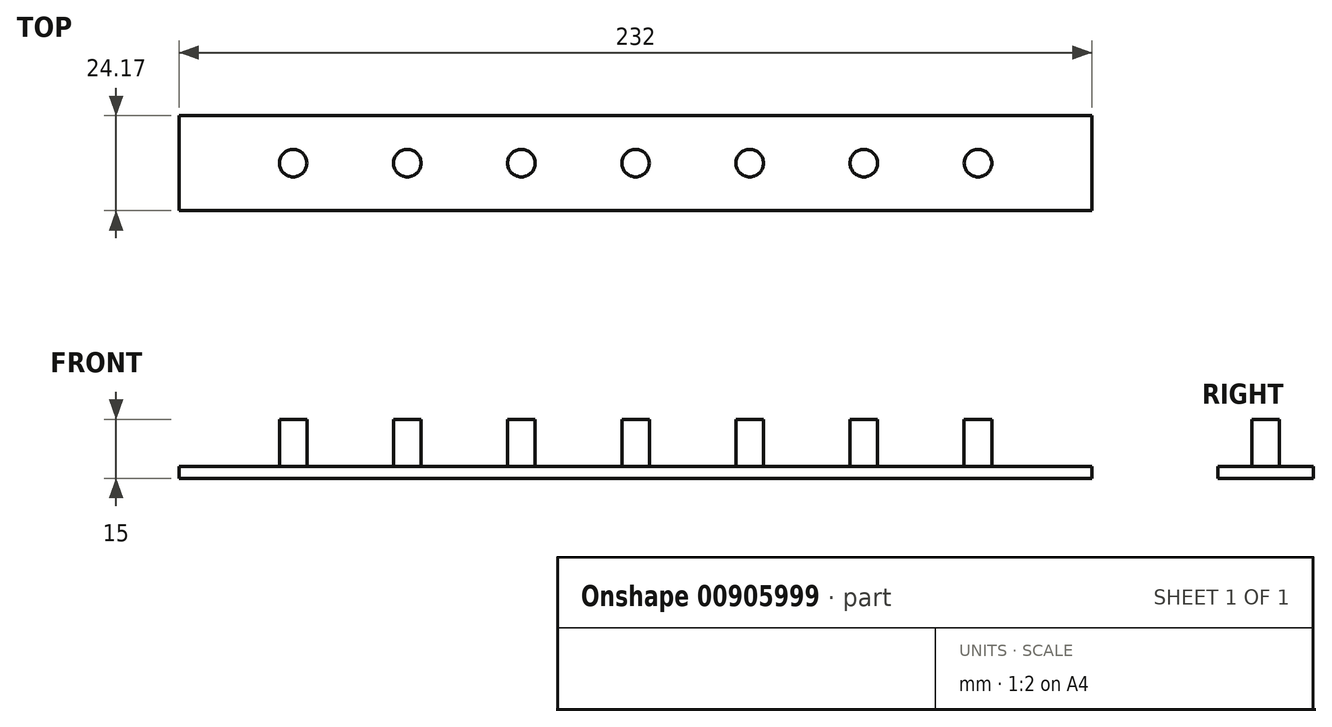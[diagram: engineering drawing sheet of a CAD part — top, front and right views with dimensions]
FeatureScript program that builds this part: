
annotation { "Feature Type Name" : "Feature", "Feature Type Description" : "" }
export const myFeature = defineFeature(function(context is Context, id is Id, definition is map)
    precondition{}
    {
        {
            var Q0;
            Q0=qCreatedBy(makeId("Top.planeOp"),FACE);
            var sketch = newSketch(context, id + "F0", { "sketchPlane" : qUnion([Q0])});
            skLineSegment(sketch, "E0.bottom", {"start": v(-128.67, 31.14) * mm, "end": v(103.33, 31.14) * mm});
            skLineSegment(sketch, "E0.top", {"start": v(-128.67, 6.97) * mm, "end": v(103.33, 6.97) * mm});
            skLineSegment(sketch, "E0.left", {"start": v(-128.67, 31.14) * mm, "end": v(-128.67, 19.05) * mm});
            skLineSegment(sketch, "E0.right", {"start": v(103.33, 31.14) * mm, "end": v(103.33, 19.05) * mm});
            skLineSegment(sketch, "E1", {"start": v(-128.67, 19.05) * mm, "end": v(-128.67, 6.97) * mm});
            skLineSegment(sketch, "E2", {"start": v(103.33, 19.05) * mm, "end": v(103.33, 6.97) * mm});
            skLineSegment(sketch, "E3", {"start": v(-128.67, 19.05) * mm, "end": v(-99.67, 19.05) * mm});
            skLineSegment(sketch, "E4", {"start": v(-12.67, 19.05) * mm, "end": v(16.33, 19.05) * mm});
            skLineSegment(sketch, "E5", {"start": v(-70.67, 19.05) * mm, "end": v(-41.67, 19.05) * mm});
            skLineSegment(sketch, "E6", {"start": v(-41.67, 19.05) * mm, "end": v(-12.67, 19.05) * mm});
            skLineSegment(sketch, "E7", {"start": v(-99.67, 19.05) * mm, "end": v(-70.67, 19.05) * mm});
            skLineSegment(sketch, "E8", {"start": v(45.33, 19.05) * mm, "end": v(74.33, 19.05) * mm});
            skLineSegment(sketch, "E9", {"start": v(16.33, 19.05) * mm, "end": v(45.33, 19.05) * mm});
            skLineSegment(sketch, "E10", {"start": v(74.33, 19.05) * mm, "end": v(103.33, 19.05) * mm});
            skCircle(sketch, "E11", {"center": v(-99.67, 19.05) * mm, "radius": 3.5 * mm});
            skCircle(sketch, "E12", {"center": v(-70.67, 19.05) * mm, "radius": 3.5 * mm});
            skCircle(sketch, "E13", {"center": v(-41.67, 19.05) * mm, "radius": 3.5 * mm});
            skCircle(sketch, "E14", {"center": v(-12.67, 19.05) * mm, "radius": 3.5 * mm});
            skCircle(sketch, "E15", {"center": v(16.33, 19.05) * mm, "radius": 3.5 * mm});
            skCircle(sketch, "E16", {"center": v(45.33, 19.05) * mm, "radius": 3.5 * mm});
            skCircle(sketch, "E17", {"center": v(74.33, 19.05) * mm, "radius": 3.5 * mm});
            skSolve(sketch);
        }
        {
            var Q0;
            Q0=makeQuery(id+"F0.imprint","IMPRINT",FACE,{"disambiguationData":[TD([[makeQuery(id+"F0.imprint","IMPRINT",EDGE,{"derivedFrom":sQuery(id+"F0.wireOp",EDGE,"E0.bottom")}),-1.0]])]});
            var Q1;
            Q1=makeQuery(id+"F0.imprint","IMPRINT",FACE,{"disambiguationData":[TD([[makeQuery(id+"F0.imprint","IMPRINT",EDGE,{"derivedFrom":sQuery(id+"F0.wireOp",EDGE,"E0.top")}),1.0]])]});
            extrude(context, id + "F1", {"entities" : qUnion([Q0, Q1]), "depth" : 3 * mm, "offsetDistance" : 25 * mm});
        }
        {
            var Q0;
            {var subQ0=sQuery(id+"F0.wireOp",EDGE,"E7");var subQ1=sQuery(id+"F0.wireOp",EDGE,"E3");var subQ2=makeQuery(id+"F0.imprint","INTERSECT",VERTEX,{"derivedFrom":[subQ1,subQ0]});Q0=makeQuery(id+"F0.imprint","IMPRINT",FACE,{"disambiguationData":[TD([[makeQuery(id+"F0.imprint","IMPRINT",EDGE,{"disambiguationData":[TD([[subQ2,1.0]])],"derivedFrom":subQ1}),1.0]])]});}
            var Q1;
            {var subQ0=sQuery(id+"F0.wireOp",EDGE,"E7");var subQ1=sQuery(id+"F0.wireOp",EDGE,"E3");var subQ2=makeQuery(id+"F0.imprint","INTERSECT",VERTEX,{"derivedFrom":[subQ1,subQ0]});Q1=makeQuery(id+"F0.imprint","IMPRINT",FACE,{"disambiguationData":[TD([[makeQuery(id+"F0.imprint","IMPRINT",EDGE,{"disambiguationData":[TD([[subQ2,1.0]])],"derivedFrom":subQ1}),-1.0]])]});}
            var Q2;
            {var subQ0=sQuery(id+"F0.wireOp",EDGE,"E7");var subQ1=sQuery(id+"F0.wireOp",EDGE,"E5");var subQ2=makeQuery(id+"F0.imprint","INTERSECT",VERTEX,{"derivedFrom":[subQ1,subQ0]});Q2=makeQuery(id+"F0.imprint","IMPRINT",FACE,{"disambiguationData":[TD([[makeQuery(id+"F0.imprint","IMPRINT",EDGE,{"disambiguationData":[TD([[subQ2,-1.0]])],"derivedFrom":subQ1}),1.0]])]});}
            var Q3;
            {var subQ0=sQuery(id+"F0.wireOp",EDGE,"E7");var subQ1=sQuery(id+"F0.wireOp",EDGE,"E5");var subQ2=makeQuery(id+"F0.imprint","INTERSECT",VERTEX,{"derivedFrom":[subQ1,subQ0]});Q3=makeQuery(id+"F0.imprint","IMPRINT",FACE,{"disambiguationData":[TD([[makeQuery(id+"F0.imprint","IMPRINT",EDGE,{"disambiguationData":[TD([[subQ2,-1.0]])],"derivedFrom":subQ1}),-1.0]])]});}
            var Q4;
            {var subQ0=sQuery(id+"F0.wireOp",EDGE,"E6");var subQ1=sQuery(id+"F0.wireOp",EDGE,"E5");var subQ2=makeQuery(id+"F0.imprint","INTERSECT",VERTEX,{"derivedFrom":[subQ1,subQ0]});Q4=makeQuery(id+"F0.imprint","IMPRINT",FACE,{"disambiguationData":[TD([[makeQuery(id+"F0.imprint","IMPRINT",EDGE,{"disambiguationData":[TD([[subQ2,1.0]])],"derivedFrom":subQ1}),1.0]])]});}
            var Q5;
            {var subQ0=sQuery(id+"F0.wireOp",EDGE,"E6");var subQ1=sQuery(id+"F0.wireOp",EDGE,"E5");var subQ2=makeQuery(id+"F0.imprint","INTERSECT",VERTEX,{"derivedFrom":[subQ1,subQ0]});Q5=makeQuery(id+"F0.imprint","IMPRINT",FACE,{"disambiguationData":[TD([[makeQuery(id+"F0.imprint","IMPRINT",EDGE,{"disambiguationData":[TD([[subQ2,1.0]])],"derivedFrom":subQ1}),-1.0]])]});}
            var Q6;
            {var subQ0=sQuery(id+"F0.wireOp",EDGE,"E6");var subQ1=sQuery(id+"F0.wireOp",EDGE,"E4");var subQ2=makeQuery(id+"F0.imprint","INTERSECT",VERTEX,{"derivedFrom":[subQ1,subQ0]});Q6=makeQuery(id+"F0.imprint","IMPRINT",FACE,{"disambiguationData":[TD([[makeQuery(id+"F0.imprint","IMPRINT",EDGE,{"disambiguationData":[TD([[subQ2,-1.0]])],"derivedFrom":subQ1}),1.0]])]});}
            var Q7;
            {var subQ0=sQuery(id+"F0.wireOp",EDGE,"E6");var subQ1=sQuery(id+"F0.wireOp",EDGE,"E4");var subQ2=makeQuery(id+"F0.imprint","INTERSECT",VERTEX,{"derivedFrom":[subQ1,subQ0]});Q7=makeQuery(id+"F0.imprint","IMPRINT",FACE,{"disambiguationData":[TD([[makeQuery(id+"F0.imprint","IMPRINT",EDGE,{"disambiguationData":[TD([[subQ2,-1.0]])],"derivedFrom":subQ1}),-1.0]])]});}
            var Q8;
            {var subQ0=sQuery(id+"F0.wireOp",EDGE,"E9");var subQ1=sQuery(id+"F0.wireOp",EDGE,"E4");var subQ2=makeQuery(id+"F0.imprint","INTERSECT",VERTEX,{"derivedFrom":[subQ1,subQ0]});Q8=makeQuery(id+"F0.imprint","IMPRINT",FACE,{"disambiguationData":[TD([[makeQuery(id+"F0.imprint","IMPRINT",EDGE,{"disambiguationData":[TD([[subQ2,1.0]])],"derivedFrom":subQ1}),1.0]])]});}
            var Q9;
            {var subQ0=sQuery(id+"F0.wireOp",EDGE,"E9");var subQ1=sQuery(id+"F0.wireOp",EDGE,"E4");var subQ2=makeQuery(id+"F0.imprint","INTERSECT",VERTEX,{"derivedFrom":[subQ1,subQ0]});Q9=makeQuery(id+"F0.imprint","IMPRINT",FACE,{"disambiguationData":[TD([[makeQuery(id+"F0.imprint","IMPRINT",EDGE,{"disambiguationData":[TD([[subQ2,1.0]])],"derivedFrom":subQ1}),-1.0]])]});}
            var Q10;
            {var subQ0=sQuery(id+"F0.wireOp",EDGE,"E9");var subQ1=sQuery(id+"F0.wireOp",EDGE,"E8");var subQ2=makeQuery(id+"F0.imprint","INTERSECT",VERTEX,{"derivedFrom":[subQ1,subQ0]});Q10=makeQuery(id+"F0.imprint","IMPRINT",FACE,{"disambiguationData":[TD([[makeQuery(id+"F0.imprint","IMPRINT",EDGE,{"disambiguationData":[TD([[subQ2,-1.0]])],"derivedFrom":subQ1}),1.0]])]});}
            var Q11;
            {var subQ0=sQuery(id+"F0.wireOp",EDGE,"E9");var subQ1=sQuery(id+"F0.wireOp",EDGE,"E8");var subQ2=makeQuery(id+"F0.imprint","INTERSECT",VERTEX,{"derivedFrom":[subQ1,subQ0]});Q11=makeQuery(id+"F0.imprint","IMPRINT",FACE,{"disambiguationData":[TD([[makeQuery(id+"F0.imprint","IMPRINT",EDGE,{"disambiguationData":[TD([[subQ2,-1.0]])],"derivedFrom":subQ1}),-1.0]])]});}
            var Q12;
            {var subQ0=sQuery(id+"F0.wireOp",EDGE,"E10");var subQ1=sQuery(id+"F0.wireOp",EDGE,"E8");var subQ2=makeQuery(id+"F0.imprint","INTERSECT",VERTEX,{"derivedFrom":[subQ1,subQ0]});Q12=makeQuery(id+"F0.imprint","IMPRINT",FACE,{"disambiguationData":[TD([[makeQuery(id+"F0.imprint","IMPRINT",EDGE,{"disambiguationData":[TD([[subQ2,1.0]])],"derivedFrom":subQ1}),1.0]])]});}
            var Q13;
            {var subQ0=sQuery(id+"F0.wireOp",EDGE,"E10");var subQ1=sQuery(id+"F0.wireOp",EDGE,"E8");var subQ2=makeQuery(id+"F0.imprint","INTERSECT",VERTEX,{"derivedFrom":[subQ1,subQ0]});Q13=makeQuery(id+"F0.imprint","IMPRINT",FACE,{"disambiguationData":[TD([[makeQuery(id+"F0.imprint","IMPRINT",EDGE,{"disambiguationData":[TD([[subQ2,1.0]])],"derivedFrom":subQ1}),-1.0]])]});}
            extrude(context, id + "F2", {"entities" : qUnion([Q0, Q1, Q2, Q3, Q4, Q5, Q6, Q7, Q8, Q9, Q10, Q11, Q12, Q13]), "operationType" : NewBodyOperationType.ADD, "depth" : 15 * mm, "offsetDistance" : 25 * mm});
        }
    });
